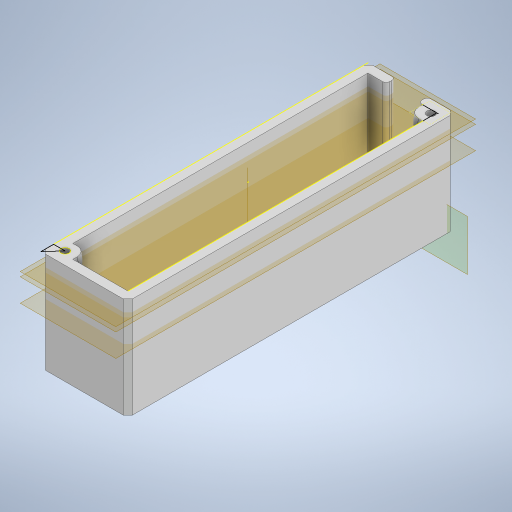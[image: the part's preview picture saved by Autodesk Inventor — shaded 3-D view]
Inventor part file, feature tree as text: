
AUTODESK INVENTOR PART (.ipt)
format: ipt  version: 2024 (Build 280153020, 153B)  size: 409,088 bytes
history: native  units: mm
features: sketch x10, extrude x6, plane x4, fillet x2, hole x1, loft x1, pattern_circular x1, chamfer x1, projected_geometry x1, other x1
ambient origin geometry x8: Origin, YZ Plane, XZ Plane, XY Plane, X Axis, Y Axis, Z Axis, Center Point
bodies: Solid1 (feature_tree)
feature tree (28):
  sketch  "Sketch1"  dims[d0=30.0mm d1=135.0mm]
  extrude  "Extrusion1"  Depth=135.0mm
  extrude  "Extrusion2"  Depth=44.0mm TaperAngle=0.0deg
  hole  "Hole1"  [1 undecoded]
  plane  "Work Plane1"
  extrude  "Extrusion3"  Depth=14.0mm
  sketch  "Sketch4"  dims[d11=80.0mm]
  extrude  "Extrusion4"  Depth=10.25mm TaperAngle=0.0deg
  plane  "Work Plane2"
  sketch  "Sketch6"  dims[d20=50.0mm d21=10.25mm d22=0.0mm]
  plane  "Work Plane3"
  sketch  "Sketch7"  dims[d31=21.0mm d32=0.0mm d33=-7.0mm d34=-10.0mm]
  sketch  "Sketch8"  dims[d35=8.0mm d36=8.0mm]
  loft  "Loft1"
  fillet  "Fillet2"  [1 undecoded]
  plane  "Work Plane4"
  sketch  "Sketch9"  dims[d39=9.0mm d40=9.0mm]
  extrude  "Extrusion5"  Depth=8.0mm
  extrude  "Extrusion6"  Depth=9.0mm
  pattern_circular  "Circular Pattern1"  Angle=90.0deg  [1 undecoded]
  fillet  "Fillet3"  [1 undecoded]
  sketch  "Sketch11"  dims[d41=0.0mm d42=90.0deg d43=0.0mm d44=90.0deg d45=0.0mm d46=90.0deg d47=4.25mm d48=-5.0mm d49=5.0mm d50=2.8194mm d51=3.5mm d52=2.75mm d53=0.0mm d54=13.0mm d55=0.0mm d56=20.0mm d57=180.0deg d59=1.5mm d60=2.0mm d61=2.0mm d62=45.0deg]
  chamfer  "Chamfer2"  Distance=4.25mm
  sketch  "Sketch2"  dims[d2=4.0mm d3=44.0mm d4=0.0mm]
  sketch  "Sketch3"  dims[d5=4.0mm d6=0.0mm d10=40.0mm]
  sketch  "Sketch5"  dims[d12=5.0mm d13=6.0mm d14=9.5mm d15=2.0mm d16=90.0deg d17=8.0mm d18=20.594885mm d19=14.0mm]
  projected_geometry  "Projected Loop1"
  other  "Work Axis1"
note: 4 required parameter values undecoded (feature->parameter linkage not recoverable at this tier; creation-order binding heuristic only, values carry confidence <= 0.55)
